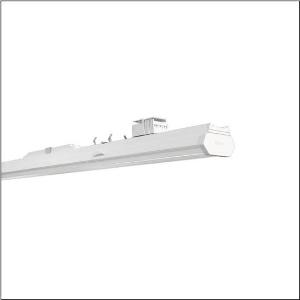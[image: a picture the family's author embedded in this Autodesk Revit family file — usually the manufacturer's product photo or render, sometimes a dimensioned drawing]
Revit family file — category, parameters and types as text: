
# Revit family: licross_11_protected_ho_51td1bdn4e5m3s4
name_source: partatom
category: Lighting Fixtures
units: mm (PartAtom-declared; Revit-internal decimal feet)

## family parameters
Cut with Voids When Loaded = No
Host = Face
Light Source = No
Part Type = Normal
Room Calculation Point = No
Round Connector Dimension = Use Diameter
Shared = No

## types (1)
- --- (1 x LED, 920 lm, 7.4 W, 4000K)
    Apparent Load = 7 VA
    CIE Flux Codes = 54 82 95 97 100
    Color Rendering = 80
    Color Temperature = 4000K
    Default Elevation = 1800 mm
    Description = Licross 11 Protected HO, luminaire insert, of sheet steel, galvanised, coil coated, white, length: 1.500mm, width: 90mm, height: 101mm, LED rated luminous flux: 14.500lm, light colour: 840, SDCM (Standard Deviation of Colour Matching)MacAdam ≤ 2 SDCM (initial), control gear: DALI 2, with plug, 6-pole, with phase selection, for trunking rail, 9 or 11-core, mains connection: 220..240V, AC, 50/60Hz, rated input power: 91W, for trunking rail, 9-/11-core, internal wiring halogen-free, for emergency light function, converter,control gear: single battery element, battery: LiFePO4, 9Ah, primary optical cover: cover, of PMMA, light emission: direct distribution, primary light characteristic: symmetric, protection rating (complete): IP54, insulation class (complete): insulation class I (protective earthing), certification: CE, UKCA, protection symbol: D if used in an environment with non-conductive dust loads with corresponding accessories, impact resistance: IK06, permissible ambient temperature for indoor applications: +5..+30°C, standard: EN 60598-2-22, LABS conformity tested according to VDMA 24364:2018-05, reducing of maximum allowable ambient temperature of 5°C with ceiling mounting, corresponds to IFS (International Featured Standards) requirements for safety and quality in the food industry, The light source and the operating device comply with the requirements of the Ecodesign Regulation (EU) 2019/2020 and are replaceable in accordance with this regulation, packaging unit: 1 piece
    Height = 92 mm
    Lamp = 1 x LED
    Lamp Light Flux = 920 lm
    Lamp Power = 7.4 W
    Lamp count = 1
    Length = 1500 mm
    Luminous efficacy = 124 lm/W
    Manufacturer = Siteco
    ModVariant = No
    Model = 51TD1BDN4E5M3S4
    Mounting Place = Ceiling
    Mounting Type = Pendant
    Number of Poles = 1
    OnlyDefault = Yes
    Power Factor = 1
    Product Name = Licross 11 Protected HO
    Product group = luminaire insert | ceiling pendant
    ProductGroupID = 901
    Protection Class = Protection class I
    Protection Degree = IP 54
    RLX_Detail_Level = 1
    RLX_Emergency_Light_Flux = 0 lm
    RLX_Emergency_Type = 0
    RLX_Emergency_Type_DB = No
    RlxData = <blob elided: 25129 chars, md5=5673006f>
    Socket = socket
    Standby Power = 0 W
    System Light Flux = 920 lm
    System Power = 7 W
    Type Comments = : emergency light operation: 3 h
    Type Image = l_1256145.jpg
    URL = http://relux.com
    VarID = @adj_096651
    Voltage = 0 V
    Weight = 0.00 kg
    Width = 88 mm

## geometry (parser evidence)
native form markers: Blend x4, Sweep x10
no freeform markers — native parametric forms only
